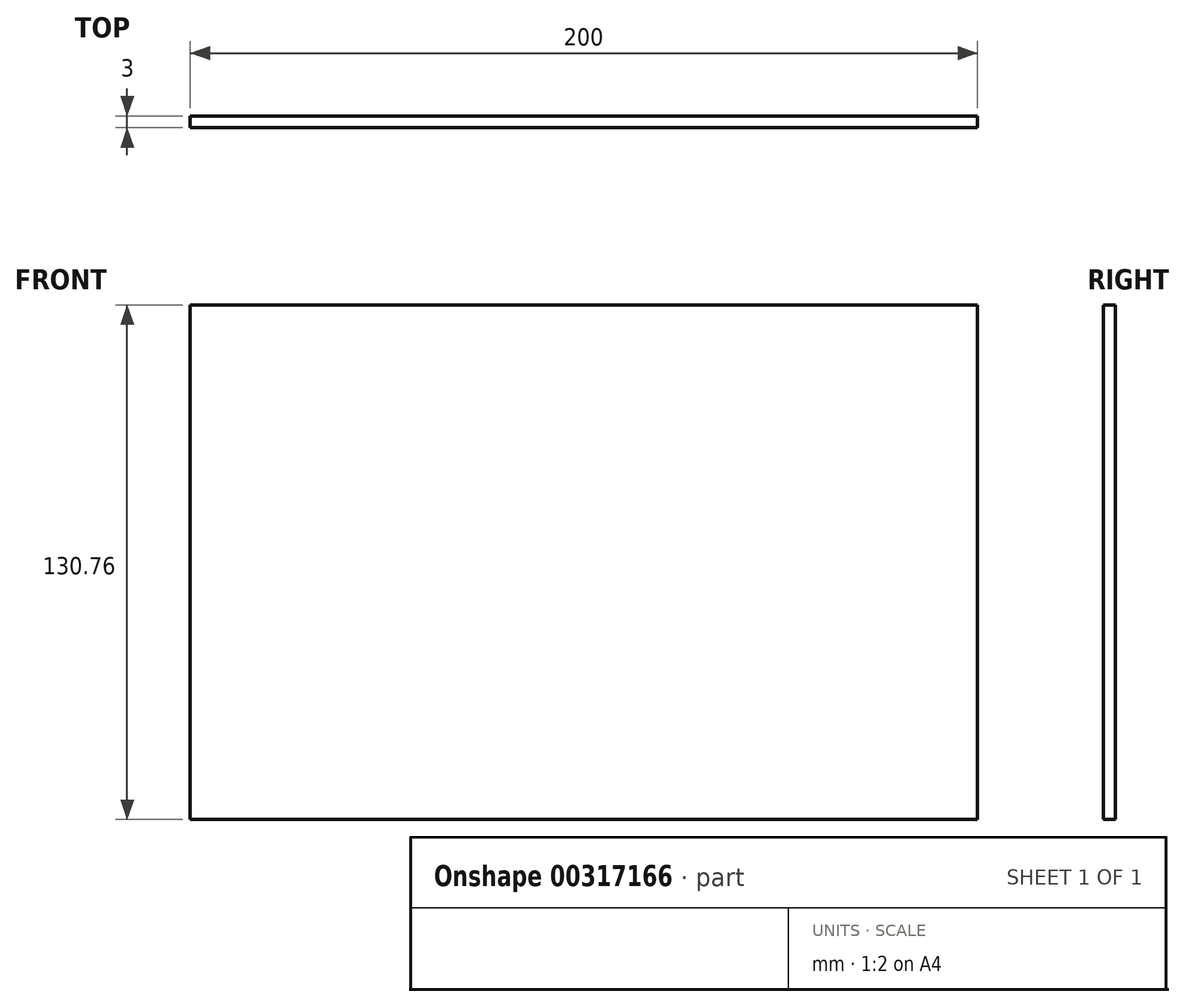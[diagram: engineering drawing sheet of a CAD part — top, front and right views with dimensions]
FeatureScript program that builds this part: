
annotation { "Feature Type Name" : "Feature", "Feature Type Description" : "" }
export const myFeature = defineFeature(function(context is Context, id is Id, definition is map)
    precondition{}
    {
        {
            var Q0;
            Q0=qCreatedBy(makeId("Front.planeOp"),FACE);
            var sketch = newSketch(context, id + "F0", { "sketchPlane" : qUnion([Q0])});
            skLineSegment(sketch, "E0.bottom", {"start": v(100, 65.38) * mm, "end": v(-100, 65.38) * mm});
            skLineSegment(sketch, "E0.top", {"start": v(100, -65.38) * mm, "end": v(-100, -65.38) * mm});
            skLineSegment(sketch, "E0.left", {"start": v(100, 65.38) * mm, "end": v(100, -65.38) * mm});
            skLineSegment(sketch, "E0.right", {"start": v(-100, 65.38) * mm, "end": v(-100, -65.38) * mm});
            skPoint(sketch, "E0.middle", {"position": v(0, 0) * mm});
            skSolve(sketch);
        }
        {
            var Q0;
            Q0=qSketchRegion(id+"F0",true);
            extrude(context, id + "F1", {"entities" : qUnion([Q0]), "depth" : 3 * mm});
        }
    });
